# Revit family: Zero U kit for universal fixing
name_source: partatom
category: Installations électriques
units: mm (PartAtom-declared; Revit-internal decimal feet)

## family parameters
Conserver l'orientation des annotations = Non
Cote de connecteur circulaire = Utiliser le diamètre
Couper avec des vides une fois chargée = Non
Hôte = Face
Partagée = Non
Point de calcul de pièce = Non
Type d'élément = Normal

## types (1)
- Zero U kit for universal fixing
    Application class = EC001130
    BIM wording = High density fiber patch panel
    Color = Steel
    Description = Zero U kit for universal fixing
    E-catalogue link = https://www.legrand.fr
    Elévation par défaut = 1219 mm
    Fabricant = LEGRAND
    Function = Patch panel fiber optic
    GTIN = 3414971939509
    General Conditions of Use = https://export.legrand.com
    Height (mm) = 64 mm  [stored 0.209974 ft]
    Legrand part number = LG-032103
    Length = 179 mm  [stored 0.58727 ft]
    Model = Zero U Kit
    Width (mm) = 216 mm  [stored 0.708661 ft]
    with SUPPORT D EPISSURE = Oui

note: [stored X ft] marks values corroborated as IEEE doubles in the binary element streams (Revit-internal decimal feet)
